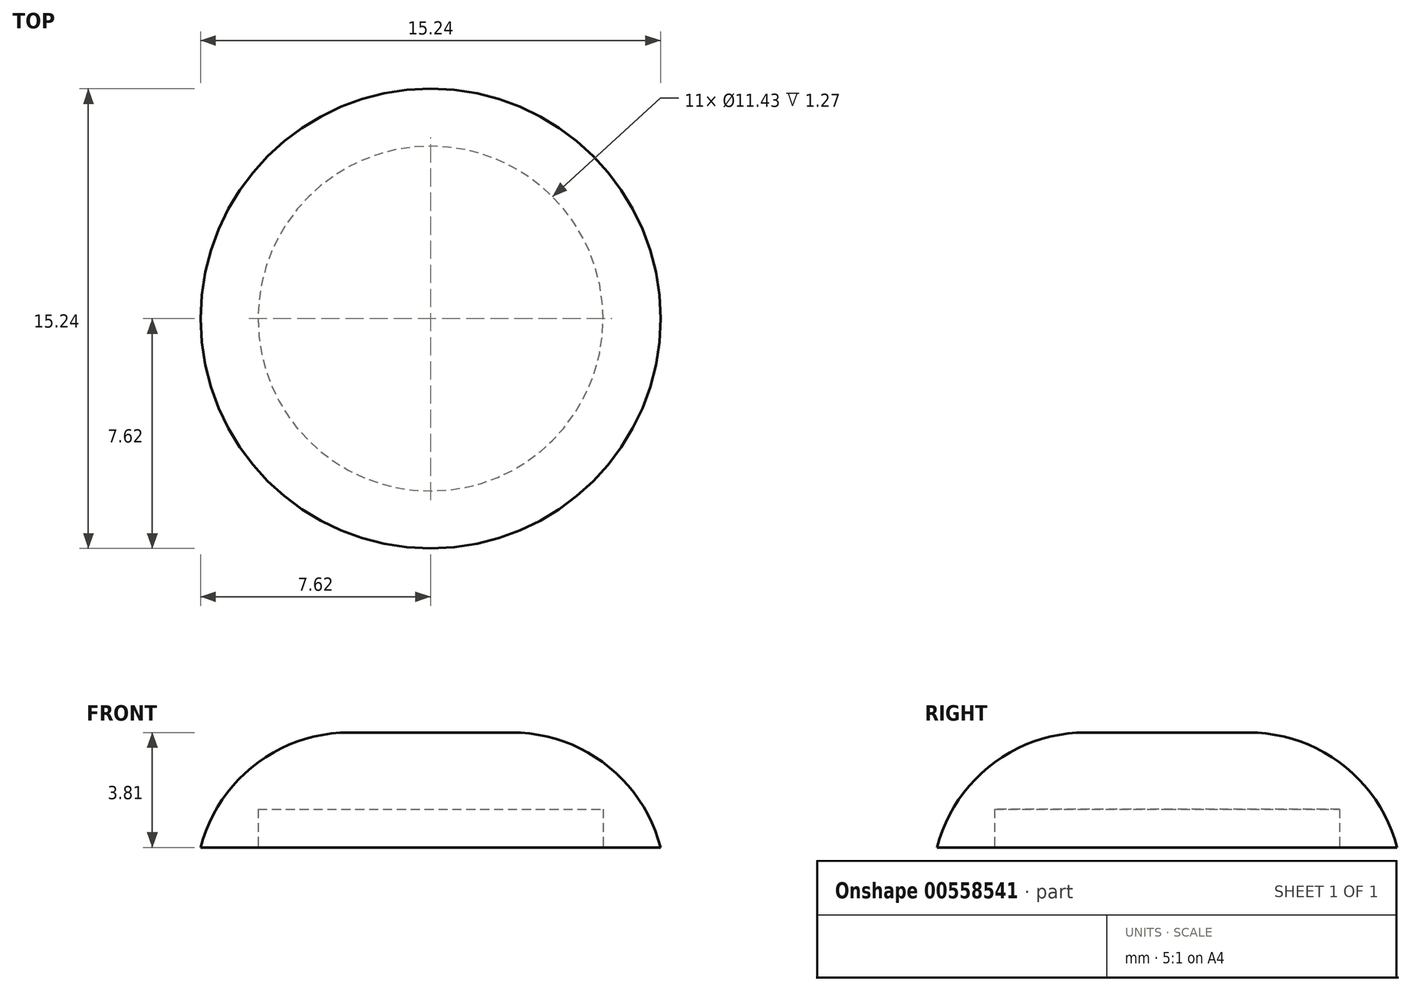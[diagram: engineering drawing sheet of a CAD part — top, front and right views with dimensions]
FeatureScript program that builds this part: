
annotation { "Feature Type Name" : "Feature", "Feature Type Description" : "" }
export const myFeature = defineFeature(function(context is Context, id is Id, definition is map)
    precondition{}
    {
        {
            var Q0;
            Q0=qCreatedBy(makeId("Top.planeOp"),FACE);
            var sketch = newSketch(context, id + "F0", { "sketchPlane" : qUnion([Q0])});
            skCircle(sketch, "E0", {"center": v(0, 0) * mm, "radius": 7.62 * mm});
            skSolve(sketch);
        }
        {
            var Q0;
            Q0=makeQuery(id+"F0.imprint","IMPRINT",FACE,{"disambiguationData":[TD([[makeQuery(id+"F0.imprint","IMPRINT",EDGE,{"derivedFrom":sQuery(id+"F0.wireOp",EDGE,"E0")}),1.0]])]});
            extrude(context, id + "F1", {"entities" : qUnion([Q0]), "depth" : 3.8 * mm, "offsetDistance" : 25.4 * mm});
        }
        {
            var Q0;
            Q0=makeQuery(id+"F1.opExtrude","CAP_EDGE",EDGE,{"disambiguationData":[OSD([sQuery(id+"F0.wireOp",EDGE,"E0")])],"isStart":false});
            fillet(context, id + "F2", {"entities" : qUnion([Q0]), "radius" : 5.08 * mm, "tangentPropagation" : true, "allowEdgeOverflow" : false});
        }
        {
            var Q0;
            Q0=makeQuery(id+"F1.opExtrude","CAP_FACE",FACE,{"disambiguationData":[OSD([sQuery(id+"F0.wireOp",EDGE,"E0")])],"isStart":true});
            var sketch = newSketch(context, id + "F3", { "sketchPlane" : qUnion([Q0])});
            skCircle(sketch, "E1", {"center": v(0, 0) * mm, "radius": 5.72 * mm});
            skSolve(sketch);
        }
        {
            var Q0;
            Q0=makeQuery(id+"F3.imprint","IMPRINT",FACE,{"disambiguationData":[TD([[makeQuery(id+"F3.imprint","IMPRINT",EDGE,{"derivedFrom":sQuery(id+"F3.wireOp",EDGE,"E1")}),1.0]])]});
            extrude(context, id + "F4", {"entities" : qUnion([Q0]), "operationType" : NewBodyOperationType.REMOVE, "oppositeDirection" : true, "depth" : 1.27 * mm, "offsetDistance" : 25.4 * mm});
        }
    });
